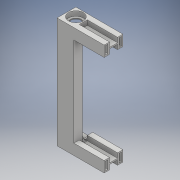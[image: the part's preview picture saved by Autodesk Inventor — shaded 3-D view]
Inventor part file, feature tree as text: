
AUTODESK INVENTOR PART (.ipt)
format: ipt  version: 2018 (Build 220112000, 112)  size: 294,912 bytes
history: native  units: mm
features: extrude x9, sketch x9, fillet x3
ambient origin geometry x8: Origin, YZ Plane, XZ Plane, XY Plane, X Axis, Y Axis, Z Axis, Center Point
bodies: Solid1 (feature_tree)
feature tree (21):
  extrude  "Extrusion1"  Depth=165.0mm
  extrude  "Extrusion2"  Depth=8.5mm
  extrude  "Extrusion3"  Depth=25.0mm TaperAngle=0.0deg
  extrude  "Extrusion4"  Depth=25.0mm
  extrude  "Extrusion5"  Depth=7.1mm
  extrude  "Extrusion6"  Depth=7.1mm TaperAngle=0.0deg
  fillet  "Fillet1"  Radius=5.0mm
  extrude  "Extrusion7"  Depth=10.0mm TaperAngle=0.0deg
  fillet  "Fillet2"  Radius=2.0mm
  extrude  "Extrusion8"  Depth=8.0mm
  extrude  "Extrusion9"  Depth=16.0mm
  fillet  "Fillet3"  Radius=8.0mm
  sketch  "Sketch1"  dims[d0=25.0mm d1=165.0mm]
  sketch  "Sketch2"  dims[d2=3.0mm d3=0.0mm d4=8.5mm]
  sketch  "Sketch3"  dims[d5=8.5mm d6=25.0mm d7=0.0mm]
  sketch  "Sketch4"  dims[d8=25.0mm d9=22.0mm]
  sketch  "Sketch5"  dims[d10=7.1mm d11=0.0mm d12=15.5mm]
  sketch  "Sketch6"  dims[d13=165.0mm d14=0.0mm d15=7.1mm d16=0.0mm d17=5.0mm]
  sketch  "Sketch7"  dims[d18=5.0mm d19=10.0mm d20=0.0mm d21=2.0mm]
  sketch  "Sketch8"  dims[d22=16.0mm d23=8.0mm]
  sketch  "Sketch9"  dims[d24=16.0mm d25=16.0mm d26=8.0mm d27=45.0mm d28=0.0mm d29=6.0mm d30=12.25mm d31=3.5mm d32=12.25mm d33=3.5mm d34=12.25mm d35=12.25mm d36=3.5mm d37=40.0mm d38=0.0mm d39=1.0mm d40=2.0mm d41=8.0mm d42=1.0mm d43=2.0mm d44=12.0mm d45=0.0mm d46=6.0mm]
